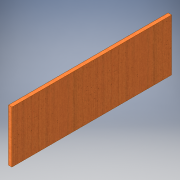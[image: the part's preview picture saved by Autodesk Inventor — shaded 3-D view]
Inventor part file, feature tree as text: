
AUTODESK INVENTOR PART (.ipt)
format: ipt  version: 2016 (Build 200138000, 138)  size: 104,448 bytes
history: native  units: in
note: dims shown in document units (in); Inventor stores cm internally (conversion verified against a paired STEP export)
features: extrude x1, sketch x1
ambient origin geometry x8: Origin, YZ Plane, XZ Plane, XY Plane, X Axis, Y Axis, Z Axis, Center Point
bodies: Solid1 (feature_tree)
feature tree (2):
  extrude  "Extrusion1"  Depth=6.5in
  sketch  "Sketch1"  dims[d0=20.0in d1=6.5in d2=0.4375in d3=0.0in]
